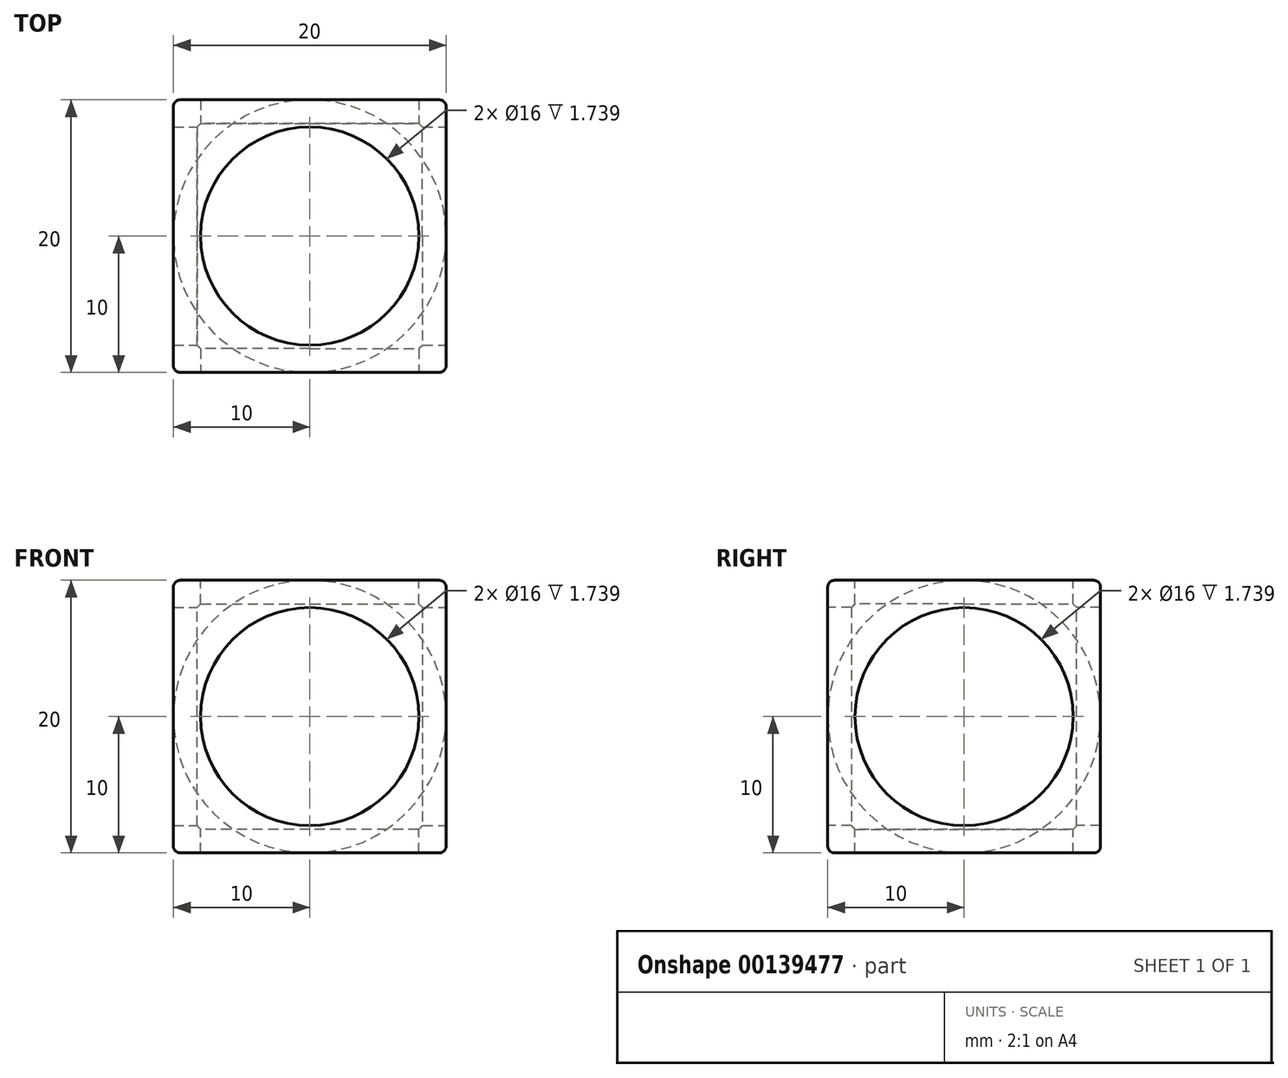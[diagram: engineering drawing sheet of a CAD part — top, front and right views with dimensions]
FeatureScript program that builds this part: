
annotation { "Feature Type Name" : "Feature", "Feature Type Description" : "" }
export const myFeature = defineFeature(function(context is Context, id is Id, definition is map)
    precondition{}
    {
        {
            var Q0;
            Q0=qCreatedBy(makeId("Top.planeOp"),FACE);
            var sketch = newSketch(context, id + "F0", { "sketchPlane" : qUnion([Q0])});
            skLineSegment(sketch, "E0.bottom", {"start": v(-10, 10) * mm, "end": v(10, 10) * mm});
            skLineSegment(sketch, "E0.top", {"start": v(-10, -10) * mm, "end": v(10, -10) * mm});
            skLineSegment(sketch, "E0.left", {"start": v(-10, 10) * mm, "end": v(-10, -10) * mm});
            skLineSegment(sketch, "E0.right", {"start": v(10, 10) * mm, "end": v(10, -10) * mm});
            skSolve(sketch);
        }
        {
            var Q0;
            Q0=makeQuery(id+"F0.imprint","IMPRINT",FACE,{"disambiguationData":[TD([[makeQuery(id+"F0.imprint","IMPRINT",EDGE,{"derivedFrom":sQuery(id+"F0.wireOp",EDGE,"E0.bottom")}),-1.0]])]});
            extrude(context, id + "F1", {"entities" : qUnion([Q0]), "endBound" : BoundingType.SYMMETRIC, "depth" : 20 * mm});
        }
        {
            var Q0;
            Q0=makeQuery(id+"F1.opExtrude","SWEPT_FACE",FACE,{"disambiguationData":[OSD([sQuery(id+"F0.wireOp",EDGE,"E0.top")])]});
            var sketch = newSketch(context, id + "F2", { "sketchPlane" : qUnion([Q0])});
            skCircle(sketch, "E1", {"center": v(0, 0) * mm, "radius": 8 * mm});
            skSolve(sketch);
        }
        {
            var Q0;
            Q0=qSketchRegion(id+"F2",true);
            extrude(context, id + "F3", {"entities" : qUnion([Q0]), "operationType" : NewBodyOperationType.REMOVE, "endBound" : BoundingType.THROUGH_ALL, "oppositeDirection" : true, "depth" : 25 * mm});
        }
        {
            var Q0;
            Q0=makeQuery(id+"F1.opExtrude","CAP_FACE",FACE,{"disambiguationData":[OSD([sQuery(id+"F0.wireOp",EDGE,"E0.bottom"),sQuery(id+"F0.wireOp",EDGE,"E0.top"),sQuery(id+"F0.wireOp",EDGE,"E0.left"),sQuery(id+"F0.wireOp",EDGE,"E0.right")])],"isStart":false});
            var sketch = newSketch(context, id + "F4", { "sketchPlane" : qUnion([Q0])});
            skCircle(sketch, "E2", {"center": v(0, 0) * mm, "radius": 8 * mm});
            skSolve(sketch);
        }
        {
            var Q0;
            Q0=qSketchRegion(id+"F4",true);
            extrude(context, id + "F5", {"entities" : qUnion([Q0]), "operationType" : NewBodyOperationType.REMOVE, "endBound" : BoundingType.THROUGH_ALL, "oppositeDirection" : true, "depth" : 25 * mm});
        }
        {
            var Q0;
            Q0=makeQuery(id+"F1.opExtrude","SWEPT_FACE",FACE,{"disambiguationData":[OSD([sQuery(id+"F0.wireOp",EDGE,"E0.right")])]});
            var sketch = newSketch(context, id + "F6", { "sketchPlane" : qUnion([Q0])});
            skCircle(sketch, "E3", {"center": v(0, 0) * mm, "radius": 8 * mm});
            skSolve(sketch);
        }
        {
            var Q0;
            Q0=makeQuery(id+"F6.imprint","IMPRINT",FACE,{"disambiguationData":[TD([[makeQuery(id+"F6.imprint","IMPRINT",EDGE,{"derivedFrom":sQuery(id+"F6.wireOp",EDGE,"E3")}),1.0]])]});
            var Q1;
            Q1=sQuery(id+"F6.wireOp",EDGE,"E3");
            extrude(context, id + "F7", {"entities" : qUnion([Q0]), "operationType" : NewBodyOperationType.REMOVE, "surfaceEntities" : qUnion([Q1]), "endBound" : BoundingType.THROUGH_ALL, "oppositeDirection" : true, "depth" : 25 * mm});
        }
        {
            var Q0;
            Q0=qCreatedBy(makeId("Top.planeOp"),FACE);
            var sketch = newSketch(context, id + "F8", { "sketchPlane" : qUnion([Q0])});
            skCircle(sketch, "E4", {"center": v(0, 0) * mm, "radius": 11.5 * mm});
            skLineSegment(sketch, "E5", {"start": v(0, 11.5) * mm, "end": v(0, -11.5) * mm});
            skSolve(sketch);
        }
        {
            var Q0;
            {var subQ0=sQuery(id+"F8.wireOp",EDGE,"E5");Q0=makeQuery(id+"F8.imprint","IMPRINT",FACE,{"disambiguationData":[TD([[makeQuery(id+"F8.imprint","IMPRINT",EDGE,{"derivedFrom":subQ0}),-1.0]])]});}
            var Q1;
            Q1=sQuery(id+"F8.wireOp",EDGE,"E5");
            revolve(context, id + "F9", {"operationType" : NewBodyOperationType.REMOVE, "entities" : qUnion([Q0]), "axis" : qUnion([Q1]), "revolveType" : RevolveType.FULL, "oppositeDirection" : true});
        }
        {
            var Q0;
            Q0=qCreatedBy(makeId("Top.planeOp"),FACE);
            var sketch = newSketch(context, id + "F10", { "sketchPlane" : qUnion([Q0])});
            skCircle(sketch, "E6", {"center": v(0, 0) * mm, "radius": 10 * mm});
            skLineSegment(sketch, "E7", {"start": v(0, 10) * mm, "end": v(0, -10) * mm});
            skSolve(sketch);
        }
        {
            var Q0;
            {var subQ0=sQuery(id+"F10.wireOp",EDGE,"E7");Q0=makeQuery(id+"F10.imprint","IMPRINT",FACE,{"disambiguationData":[TD([[makeQuery(id+"F10.imprint","IMPRINT",EDGE,{"derivedFrom":subQ0}),1.0]])]});}
            var Q1;
            Q1=sQuery(id+"F10.wireOp",EDGE,"E7");
            revolve(context, id + "F11", {"entities" : qUnion([Q0]), "axis" : qUnion([Q1]), "revolveType" : RevolveType.FULL});
        }
        {
            var Q0;
            Q0=makeQuery(id+"F1.opExtrude","CAP_EDGE",EDGE,{"disambiguationData":[OSD([sQuery(id+"F0.wireOp",EDGE,"E0.top")])],"isStart":false});
            var Q1;
            Q1=makeQuery(id+"F1.opExtrude","CAP_EDGE",EDGE,{"disambiguationData":[OSD([sQuery(id+"F0.wireOp",EDGE,"E0.left")])],"isStart":false});
            var Q2;
            Q2=makeQuery(id+"F1.opExtrude","CAP_EDGE",EDGE,{"disambiguationData":[OSD([sQuery(id+"F0.wireOp",EDGE,"E0.bottom")])],"isStart":false});
            var Q3;
            Q3=makeQuery(id+"F1.opExtrude","CAP_EDGE",EDGE,{"disambiguationData":[OSD([sQuery(id+"F0.wireOp",EDGE,"E0.right")])],"isStart":false});
            var Q4;
            Q4=makeQuery(id+"F1.opExtrude","SWEPT_EDGE",EDGE,{"disambiguationData":[OSD([sQuery(id+"F0.wireOp",EDGE,"E0.bottom"),sQuery(id+"F0.wireOp",EDGE,"E0.right")])]});
            var Q5;
            Q5=makeQuery(id+"F1.opExtrude","CAP_EDGE",EDGE,{"disambiguationData":[OSD([sQuery(id+"F0.wireOp",EDGE,"E0.right")])],"isStart":true});
            var Q6;
            Q6=makeQuery(id+"F1.opExtrude","SWEPT_EDGE",EDGE,{"disambiguationData":[OSD([sQuery(id+"F0.wireOp",EDGE,"E0.top"),sQuery(id+"F0.wireOp",EDGE,"E0.right")])]});
            var Q7;
            Q7=makeQuery(id+"F1.opExtrude","CAP_EDGE",EDGE,{"disambiguationData":[OSD([sQuery(id+"F0.wireOp",EDGE,"E0.top")])],"isStart":true});
            var Q8;
            Q8=makeQuery(id+"F1.opExtrude","SWEPT_EDGE",EDGE,{"disambiguationData":[OSD([sQuery(id+"F0.wireOp",EDGE,"E0.top"),sQuery(id+"F0.wireOp",EDGE,"E0.left")])]});
            var Q9;
            Q9=makeQuery(id+"F1.opExtrude","CAP_EDGE",EDGE,{"disambiguationData":[OSD([sQuery(id+"F0.wireOp",EDGE,"E0.bottom")])],"isStart":true});
            var Q10;
            Q10=makeQuery(id+"F1.opExtrude","SWEPT_EDGE",EDGE,{"disambiguationData":[OSD([sQuery(id+"F0.wireOp",EDGE,"E0.bottom"),sQuery(id+"F0.wireOp",EDGE,"E0.left")])]});
            var Q11;
            Q11=makeQuery(id+"F1.opExtrude","CAP_EDGE",EDGE,{"disambiguationData":[OSD([sQuery(id+"F0.wireOp",EDGE,"E0.left")])],"isStart":true});
            fillet(context, id + "F12", {"entities" : qUnion([Q0, Q1, Q2, Q3, Q4, Q5, Q6, Q7, Q8, Q9, Q10, Q11]), "radius" : 0.5 * mm, "tangentPropagation" : true, "allowEdgeOverflow" : false});
        }
    });
